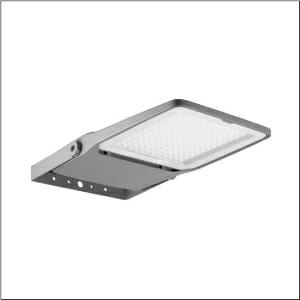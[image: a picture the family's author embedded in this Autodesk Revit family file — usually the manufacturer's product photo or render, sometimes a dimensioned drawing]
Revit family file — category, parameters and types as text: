
# Revit family: floodlight_fl_20_midi___pl61_5xa7682e2c2ac_53d1
name_source: partatom
category: Lighting Fixtures
units: mm (PartAtom-declared; Revit-internal decimal feet)

## family parameters
Cut with Voids When Loaded = No
Host = Face
Light Source = No
Part Type = Normal
Room Calculation Point = No
Round Connector Dimension = Use Diameter
Shared = No

## types (1)
- --- (1 x LED 4000K / CRI = 70 (unbekannt), 27150 lm, 4000K)
    Apparent Load = 208 VA
    CIE Flux Codes = 33 65 98 100 100
    Color Rendering = 70
    Color Temperature = 4000K
    Default Elevation = 1800 mm
    Description = Floodlight FL 20 midi, floodlight, primary light control with lens, of plastic, primary optical cover: protective disc, of toughened safety glass, transparent, light distribution: PL61, light emission: direct distribution, primary light characteristic: asymmetric, installation type: surface-mounted, LED, High Power LED, rated luminous flux: 27.150lm, luminous efficacy: 131lm/W, light colour: 740, colour temperature: 4000K, control gear: ECG Plus, control: flexible luminous flux parameterisation, time-dependent luminous flux control, digital communication interface, power reduction, overheat protection, electronic power reduction, with terminal, 5-pole, max. 2.5mm², mains connection: 220..240V, AC, 50/60Hz, rated input power: 208W, LED unit, of diecast aluminium, powder-coated, Siteco® metallic grey (DB 702S), corrosivity category C5 mid according to DIN EN ISO 12944, incl. 1x M20 cable gland for cable Ø 6.5..12mm, length: 731mm, width: 450mm, height: 76mm, housing frame, of diecast aluminium, powder-coated, Siteco® metallic grey (DB 702S), wall fastening, of steel, powder-coated, Siteco® metallic grey (DB 702S), DALI, protection rating (complete): IP66, insulation class (complete): insulation class II (safety insulation), certification: CE, ENEC, VDE, protection symbol: D, permissible operating ambient temperature: -40..+40°C, permissible operating ambient temperature for outdoor applications: -40..+50°C, standard: DIN EN 12944, packaging unit: 1 piece

Light Distribution: PL61
    Height = 76 mm
    Lamp = 1 x LED 4000K / CRI >= 70 (unbekannt)
    Lamp Light Flux = 27150 lm
    Lamp count = 1
    Length = 731 mm
    Luminous efficacy = 131 lm/W
    Manufacturer = Siteco
    ModVariant = No
    Model = 5XA7682E2C2AC
    Mounting Place = Wall
    Mounting Type = Surface mounted
    Number of Poles = 1
    OnlyDefault = Yes
    Power Factor = 1
    Product Name = Floodlight FL 20 midi | PL61
    Product group = floodlight | wall mounted
    ProductGroupID = 2001
    Protection Class = Protection class II
    Protection Degree = IP 66
    RLX_Detail_Level = 1
    RLX_Emergency_Light_Flux = 0 lm
    RLX_Emergency_Type = 0
    RLX_Emergency_Type_DB = No
    RlxData = <blob elided: 92289 chars, md5=42169379>
    Socket = socket
    Standby Power = 0 W
    System Light Flux = 27150 lm
    System Power = 208 W
    Type Comments = factory setting: luminous flux: 100 % | dim-lin: 254 | 484 mA
    Type Image = l_1005944.jpg
    URL = http://relux.com
    VarID = @adj_146917
    Voltage = 0 V
    Weight = 0.00 kg
    Width = 450 mm

## geometry (parser evidence)
native form markers: Blend x4, Sweep x15
no freeform markers — native parametric forms only
